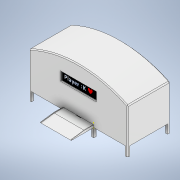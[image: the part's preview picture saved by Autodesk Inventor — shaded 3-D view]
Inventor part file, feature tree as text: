
AUTODESK INVENTOR PART (.ipt)
format: ipt  version: 2021 (Build 250183000, 183)  size: 635,904 bytes
history: native  units: mm
features: sketch x30, extrude x27, chamfer x3, fillet x2, other x2, plane x1
ambient origin geometry x8: Origin, YZ Plane, XZ Plane, XY Plane, X Axis, Y Axis, Z Axis, Center Point
bodies: Solid1 (feature_tree)
feature tree (65):
  extrude  "Extrusion1"  Depth=68.5mm
  extrude  "Extrusion2"  Depth=5.0mm
  extrude  "Extrusion3"  Depth=5.0mm TaperAngle=0.0deg
  extrude  "Extrusion4"  Depth=5.0mm
  extrude  "Extrusion5"  Depth=2.5mm
  extrude  "Extrusion6"  Depth=86.5mm
  extrude  "Extrusion7"  Depth=1.1mm
  extrude  "Extrusion8"  Depth=5.0mm TaperAngle=0.0deg
  extrude  "Extrusion9"  Depth=30.0mm TaperAngle=0.0deg
  extrude  "Extrusion13"  Depth=2.3mm
  extrude  "Extrusion14"  Depth=2.3mm
  fillet  "Fillet1"  Radius=50.0mm
  extrude  "Extrusion16"  Depth=68.5mm TaperAngle=0.0deg
  extrude  "Extrusion17"  Depth=1.0mm TaperAngle=0.0deg
  sketch  "Sketch23"  dims[d40=1.0mm d41=0.0mm d56=1.1mm]
  extrude  "Extrusion18"  Depth=1.1mm
  extrude  "Extrusion19"  Depth=20.0mm TaperAngle=0.0deg
  extrude  "Extrusion20"  Depth=2.3mm
  extrude  "Extrusion21"  Depth=5.0mm
  sketch  "Sketch29"  dims[d81=5.0mm d82=30.0mm d83=0.0mm]
  extrude  "Extrusion22"  Depth=20.0mm
  extrude  "Extrusion23"  Depth=30.0mm TaperAngle=0.0deg
  chamfer  "Chamfer1"  Distance=20.0mm
  extrude  "Extrusion25"  Depth=5.0mm
  extrude  "Extrusion26"  Depth=20.0mm TaperAngle=0.0deg
  extrude  "Extrusion27"  Depth=75.0mm TaperAngle=0.0deg
  extrude  "Extrusion28"  Depth=5.0mm
  fillet  "Fillet2"  Radius=5.0mm
  extrude  "Extrusion29"  Depth=5.0mm
  extrude  "Extrusion30"  Depth=20.0mm TaperAngle=0.0deg
  extrude  "Extrusion31"  Depth=5.0mm
  chamfer  "Chamfer2"  Distance=5.0mm
  chamfer  "Chamfer3"  Distance=5.0mm
  extrude  "Extrusion32"  Depth=2.2mm TaperAngle=0.0deg
  plane  "Work Plane1"
  other  "Decal1"
  sketch  "Sketch1"  dims[d0=94.0mm d1=68.5mm]
  sketch  "Sketch2"  dims[d2=4.0mm d3=0.0mm d4=5.0mm]
  sketch  "Sketch3"  dims[d5=10.0mm d6=5.0mm d7=0.0mm]
  sketch  "Sketch4"  dims[d8=5.0mm d9=5.0mm]
  sketch  "Sketch5"  dims[d11=2.5mm d12=2.5mm]
  sketch  "Sketch6"  dims[d13=2.5mm d15=86.5mm]
  sketch  "Sketch8"  dims[d16=5.0mm d17=0.0mm d19=1.1mm]
  sketch  "Sketch10"  dims[d20=1.1mm d21=5.0mm d22=0.0mm]
  sketch  "Sketch11"  dims[d23=2.5mm d24=30.0mm d25=0.0mm]
  sketch  "Sketch15"  dims[d26=2.3mm d27=2.3mm]
  sketch  "Sketch17"  dims[d28=2.3mm d29=2.3mm d30=50.0mm d31=0.0mm]
  sketch  "Sketch19"  dims[d32=20.0mm d34=68.5mm d35=0.0mm]
  sketch  "Sketch21"  dims[d37=1.1mm d38=1.0mm d39=0.0mm]
  sketch  "Sketch24"  dims[d57=94.0mm d58=0.0mm d69=20.0mm d70=0.0mm]
  sketch  "Sketch25"  dims[d75=10.0mm d76=2.3mm]
  sketch  "Sketch26"  dims[d77=10.0mm d78=5.0mm]
  sketch  "Sketch28"  dims[d79=20.0mm d80=5.0mm]
  sketch  "Sketch30"  dims[d84=5.0mm]
  sketch  "Sketch32"  dims[d85=5.0mm d90=20.0mm d91=0.0mm]
  sketch  "Sketch34"  dims[d94=5.0mm d95=5.0mm]
  sketch  "Sketch35"  dims[d96=5.0mm d97=20.0mm d98=0.0mm]
  sketch  "Sketch36"  dims[d99=75.0mm d100=0.0mm d101=75.0mm d102=0.0mm]
  sketch  "Sketch37"  dims[d103=5.0mm d104=5.0mm d105=5.0mm]
  sketch  "Sketch38"  dims[d106=5.0mm d107=5.0mm]
  sketch  "Sketch39"  dims[d108=5.0mm d109=20.0mm d110=0.0mm]
  sketch  "Sketch40"  dims[d111=5.0mm d112=5.0mm]
  sketch  "Sketch41"  dims[d113=5.0mm]
  sketch  "Sketch43"  dims[d114=5.0mm d115=5.0mm d116=5.0mm d117=0.0mm d120=30.0mm d121=0.0mm d126=2.0mm d127=2.0mm d128=45.0deg d129=2.5mm d130=68.0mm d131=0.0mm d132=68.0mm d133=0.0mm d134=20.0mm d135=10.0mm d136=42.117007mm d137=28.65mm d138=20.0mm d139=42.117007mm d140=28.65mm d141=2.5mm d142=0.0mm d143=5.0mm d144=20.0mm d145=20.0mm d146=0.0mm d147=10.0mm d148=5.0mm d149=5.0mm d150=5.0mm d151=0.0mm d153=2.3mm d154=2.3mm d155=2.3mm d156=40.0mm d157=0.0mm d158=250.0mm d159=94.0mm d160=0.0mm d161=2.0mm d162=2.0mm d163=45.0deg d164=2.0mm d165=2.0mm d166=45.0deg d170=40.0mm d171=20.0mm d172=40.0mm d173=20.0mm d174=2.2mm d175=0.0mm d176=30.25mm d71=0.5mm d72=0.872665mm]
  other  "Image1"
